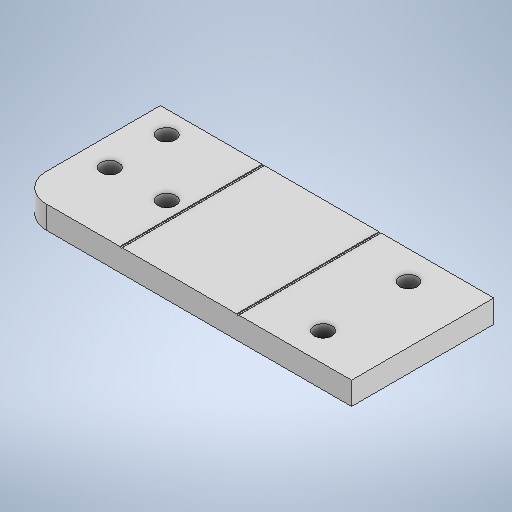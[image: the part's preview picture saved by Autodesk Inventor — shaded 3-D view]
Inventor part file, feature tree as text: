
AUTODESK INVENTOR PART (.ipt)
format: ipt  version: 2025 (Build 290162000, 162)  size: 257,536 bytes
history: native  units: mm
features: sketch x5, extrude x2, fillet x2
ambient origin geometry x8: Origin, YZ Plane, XZ Plane, XY Plane, X Axis, Y Axis, Z Axis, Center Point
bodies: Solid1 (feature_tree)
feature tree (9):
  extrude  "Extrusion1"  Depth=3.9mm
  extrude  "Extrusion2"  Depth=10.0mm
  fillet  "Fillet1"  Radius=25.0mm
  fillet  "Fillet2"  Radius=5.0mm
  sketch  "Sketch1"  dims[d0=3.1mm d1=3.9mm]
  sketch  "Sketch Rectangular Pattern1"  dims[d2=20.0mm d4=10.0mm d5=10.0mm d7=10.0mm d9=20.0mm d11=10.0mm d12=10.0mm d14=10.0mm d16=25.0mm d17=5.0mm]
  sketch  "Sketch Rectangular Pattern2"  dims[d18=58.58mm]
  sketch  "Sketch Rectangular Pattern3"  dims[d20=10.0mm d21=20.0mm d23=15.0mm d24=10.0mm d26=10.0mm d28=5.0mm d29=4.0mm d30=0.0mm d31=0.25mm d32=4.0mm d33=0.0mm d34=18.085mm d35=0.25mm d36=20.0mm d37=0.1mm d38=5.0mm]
  sketch  "Sketch2"  dims[d19=3.1mm]
